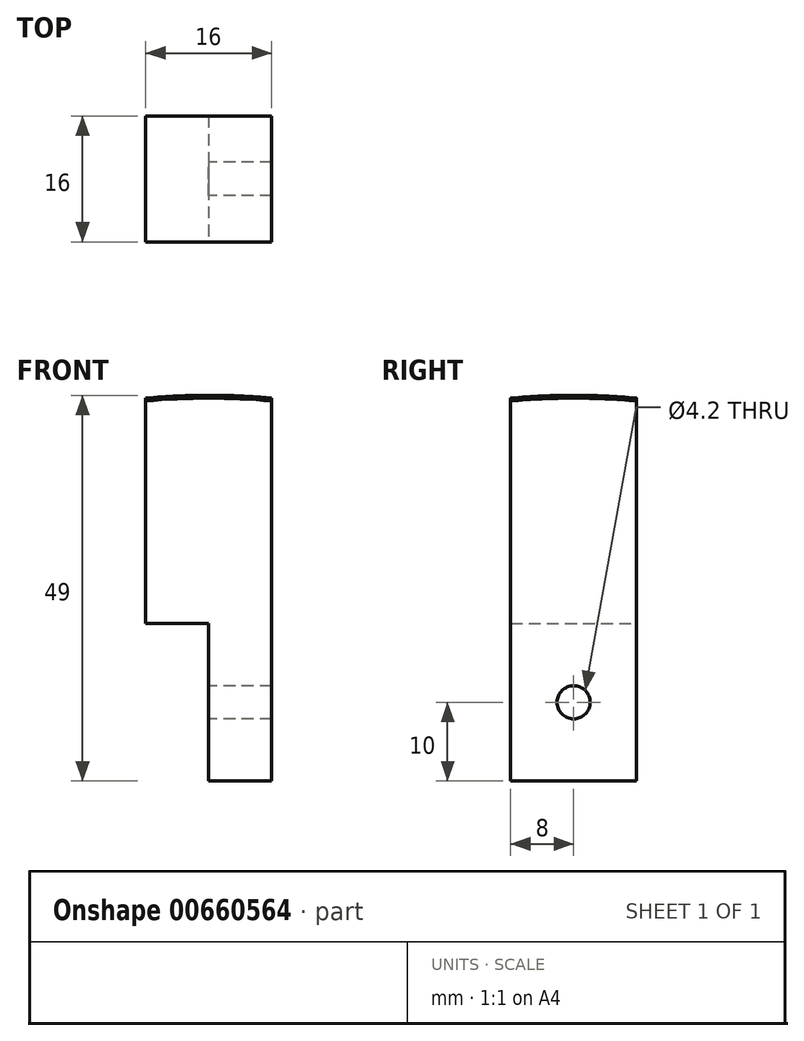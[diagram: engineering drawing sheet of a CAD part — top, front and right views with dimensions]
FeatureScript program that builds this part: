
annotation { "Feature Type Name" : "Feature", "Feature Type Description" : "" }
export const myFeature = defineFeature(function(context is Context, id is Id, definition is map)
    precondition{}
    {
        {
            var Q0;
            Q0=qCreatedBy(makeId("Front.planeOp"),FACE);
            var sketch = newSketch(context, id + "F0", { "sketchPlane" : qUnion([Q0])});
            skArc(sketch, "E0", {"start": v(0, 89) * mm, "mid": v(-89, 0) * mm, "end": v(0, -89) * mm});
            skLineSegment(sketch, "E1", {"start": v(0, 89) * mm, "end": v(0, -89) * mm});
            skSolve(sketch);
        }
        {
            var Q0;
            Q0=makeQuery(id+"F0.imprint","IMPRINT",FACE,{"disambiguationData":[TD([[makeQuery(id+"F0.imprint","IMPRINT",EDGE,{"derivedFrom":sQuery(id+"F0.wireOp",EDGE,"E0")}),1.0]])]});
            var Q1;
            Q1=sQuery(id+"F0.wireOp",EDGE,"E1");
            revolve(context, id + "F1", {"entities" : qUnion([Q0]), "axis" : qUnion([Q1]), "revolveType" : RevolveType.FULL});
        }
        {
            var Q0;
            Q0=qCreatedBy(makeId("Top.planeOp"),FACE);
            var sketch = newSketch(context, id + "F2", { "sketchPlane" : qUnion([Q0])});
            skLineSegment(sketch, "E2.bottom", {"start": v(-8, -8) * mm, "end": v(8, -8) * mm});
            skLineSegment(sketch, "E2.top", {"start": v(-8, 8) * mm, "end": v(8, 8) * mm});
            skLineSegment(sketch, "E2.left", {"start": v(-8, -8) * mm, "end": v(-8, 8) * mm});
            skLineSegment(sketch, "E2.right", {"start": v(8, -8) * mm, "end": v(8, 8) * mm});
            skLineSegment(sketch, "E3", {"start": v(0, 0) * mm, "end": v(0, -32.26) * mm, "construction": true});
            skLineSegment(sketch, "E4", {"start": v(0, 0) * mm, "end": v(-29.45, 0) * mm, "construction": true});
            skSolve(sketch);
        }
        {
            var Q0;
            Q0 = qSketchRegion(id + "F2", true);
            extrude(context, id + "F3", {"entities" : qUnion([Q0]), "operationType" : NewBodyOperationType.INTERSECT, "depth" : 200 * mm, "offsetDistance" : 25 * mm, "symmetric" : true});
        }
        {
            var Q0;
            Q0=qCreatedBy(makeId("Front.planeOp"),FACE);
            var sketch = newSketch(context, id + "F4", { "sketchPlane" : qUnion([Q0])});
            skLineSegment(sketch, "E5.bottom", {"start": v(10, 40) * mm, "end": v(-10, 40) * mm});
            skLineSegment(sketch, "E5.top", {"start": v(10, -100) * mm, "end": v(-10, -100) * mm});
            skLineSegment(sketch, "E5.left", {"start": v(10, 40) * mm, "end": v(10, -100) * mm});
            skLineSegment(sketch, "E5.right", {"start": v(-10, 40) * mm, "end": v(-10, -100) * mm});
            skSolve(sketch);
        }
        {
            var Q0;
            Q0=makeQuery(id+"F4.imprint","IMPRINT",FACE,{"disambiguationData":[TD([[makeQuery(id+"F4.imprint","IMPRINT",EDGE,{"derivedFrom":sQuery(id+"F4.wireOp",EDGE,"E5.bottom")}),1.0]])]});
            extrude(context, id + "F5", {"entities" : qUnion([Q0]), "operationType" : NewBodyOperationType.REMOVE, "oppositeDirection" : true, "depth" : 25 * mm, "offsetDistance" : 25 * mm, "symmetric" : true});
        }
        {
            var Q0;
            Q0=qCreatedBy(makeId("Right.planeOp"),FACE);
            var sketch = newSketch(context, id + "F6", { "sketchPlane" : qUnion([Q0])});
            skLineSegment(sketch, "E6.bottom", {"start": v(8, 60) * mm, "end": v(-8, 60) * mm});
            skLineSegment(sketch, "E6.top", {"start": v(8, 40) * mm, "end": v(-8, 40) * mm});
            skLineSegment(sketch, "E6.left", {"start": v(8, 60) * mm, "end": v(8, 40) * mm});
            skLineSegment(sketch, "E6.right", {"start": v(-8, 60) * mm, "end": v(-8, 40) * mm});
            skSolve(sketch);
        }
        {
            var Q0;
            Q0 = qSketchRegion(id + "F6", true);
            extrude(context, id + "F7", {"entities" : qUnion([Q0]), "operationType" : NewBodyOperationType.REMOVE, "oppositeDirection" : true, "depth" : 25 * mm, "offsetDistance" : 25 * mm});
        }
        {
            var Q0;
            Q0=makeQuery(id+"F7.boolean.opBoolean","COPY",FACE,{"derivedFrom":makeQuery(id+"F7.opExtrude","CAP_FACE",FACE,{"disambiguationData":[OSD([sQuery(id+"F6.wireOp",EDGE,"E6.bottom"),sQuery(id+"F6.wireOp",EDGE,"E6.top"),sQuery(id+"F6.wireOp",EDGE,"E6.left"),sQuery(id+"F6.wireOp",EDGE,"E6.right")])],"isStart":true})});
            var sketch = newSketch(context, id + "F8", { "sketchPlane" : qUnion([Q0])});
            skLineSegment(sketch, "E7", {"start": v(-8, 40) * mm, "end": v(8, 60) * mm, "construction": true});
            skLineSegment(sketch, "E8", {"start": v(-8, 60) * mm, "end": v(8, 40) * mm, "construction": true});
            skPoint(sketch, "E9", {"position": v(0, 50) * mm});
            skSolve(sketch);
        }
        {
            var Q0;
            Q0=sQuery(id+"F8.wireOp",VERTEX,"E9");
            var Q1;
            Q1=makeQuery(id+"F1.opRevolve","SWEPT_BODY",BODY,{"disambiguationData":[OSD([sQuery(id+"F0.wireOp",EDGE,"E0"),sQuery(id+"F0.wireOp",EDGE,"E1")])]});
            hole(context, id + "F9", {"style" : HoleStyle.SIMPLE, "endStyle" : HoleEndStyle.THROUGH, "standardTappedOrClearance" : lookupTablePath({ "standard" : "ISO", "engagement" : "75%", "pitch" : "0.8 mm", "size" : "M5", "type" : "Tapped" }), "standardBlindInLast" : lookupTablePath({ "standard" : "ISO", "engagement" : "75%", "pitch" : "0.8 mm", "size" : "M5", "type" : "Tapped" }), "holeDiameter" : 4.2 * mm, "majorDiameter" : 5 * mm, "showTappedDepth" : true, "isTappedThrough" : true, "tappedDepth" : 12 * mm, "tapClearance" : 3, "startFromSketch" : true, "locations" : qUnion([Q0]), "scope" : qUnion([Q1])});
        }
    });
